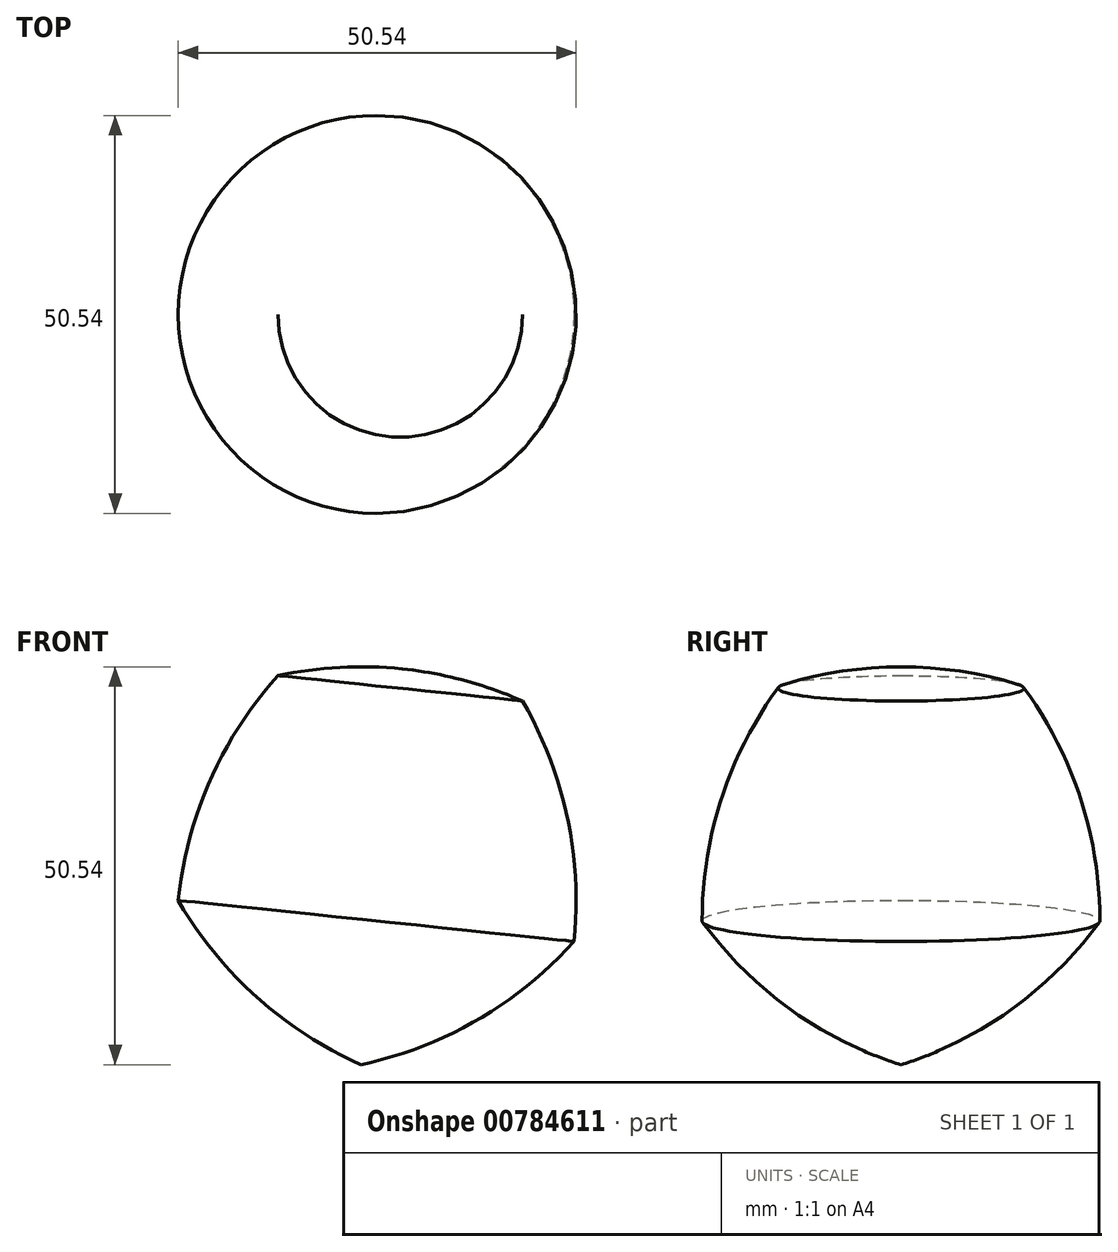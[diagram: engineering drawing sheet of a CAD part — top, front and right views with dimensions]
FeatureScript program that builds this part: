
annotation { "Feature Type Name" : "Feature", "Feature Type Description" : "" }
export const myFeature = defineFeature(function(context is Context, id is Id, definition is map)
    precondition{}
    {
        {
            var Q0;
            Q0=qCreatedBy(makeId("Front.planeOp"),FACE);
            var sketch = newSketch(context, id + "F0", { "sketchPlane" : qUnion([Q0])});
            skLineSegment(sketch, "E0.3", {"start": v(1.98, 21.4) * mm, "end": v(2.22, 21.38) * mm});
            skArc(sketch, "E1", {"start": v(-13.31, 23) * mm, "mid": v(-21.9, 9.72) * mm, "end": v(-25.98, -5.56) * mm});
            skArc(sketch, "E2", {"start": v(17.76, 19.77) * mm, "mid": v(2.48, 23.84) * mm, "end": v(-13.31, 23) * mm});
            skArc(sketch, "E3.trimOffspring", {"start": v(24.29, -10.78) * mm, "mid": v(23.44, 5.01) * mm, "end": v(17.76, 19.77) * mm});
            skArc(sketch, "E4.trimOffspring", {"start": v(-2.75, -26.43) * mm, "mid": v(12, -20.74) * mm, "end": v(24.29, -10.78) * mm});
            skArc(sketch, "E5.trimOffspring", {"start": v(-25.98, -5.56) * mm, "mid": v(-16.02, -17.83) * mm, "end": v(-2.75, -26.43) * mm});
            skLineSegment(sketch, "E6", {"start": v(-2.75, -26.43) * mm, "end": v(2.48, 23.84) * mm});
            skSolve(sketch);
        }
        {
            var Q0;
            {var subQ4=sQuery(id+"F0.wireOp",EDGE,"E1");Q0=makeQuery(id+"F0.imprint","IMPRINT",FACE,{"disambiguationData":[TD([[makeQuery(id+"F0.imprint","IMPRINT",EDGE,{"derivedFrom":subQ4}),1.0]])]});}
            var Q1;
            Q1=sQuery(id+"F0.wireOp",EDGE,"E6");
            revolve(context, id + "F1", {"surfaceOperationType" : NewSurfaceOperationType.NEW, "entities" : qUnion([Q0]), "axis" : qUnion([Q1]), "revolveType" : RevolveType.FULL});
        }
    });
